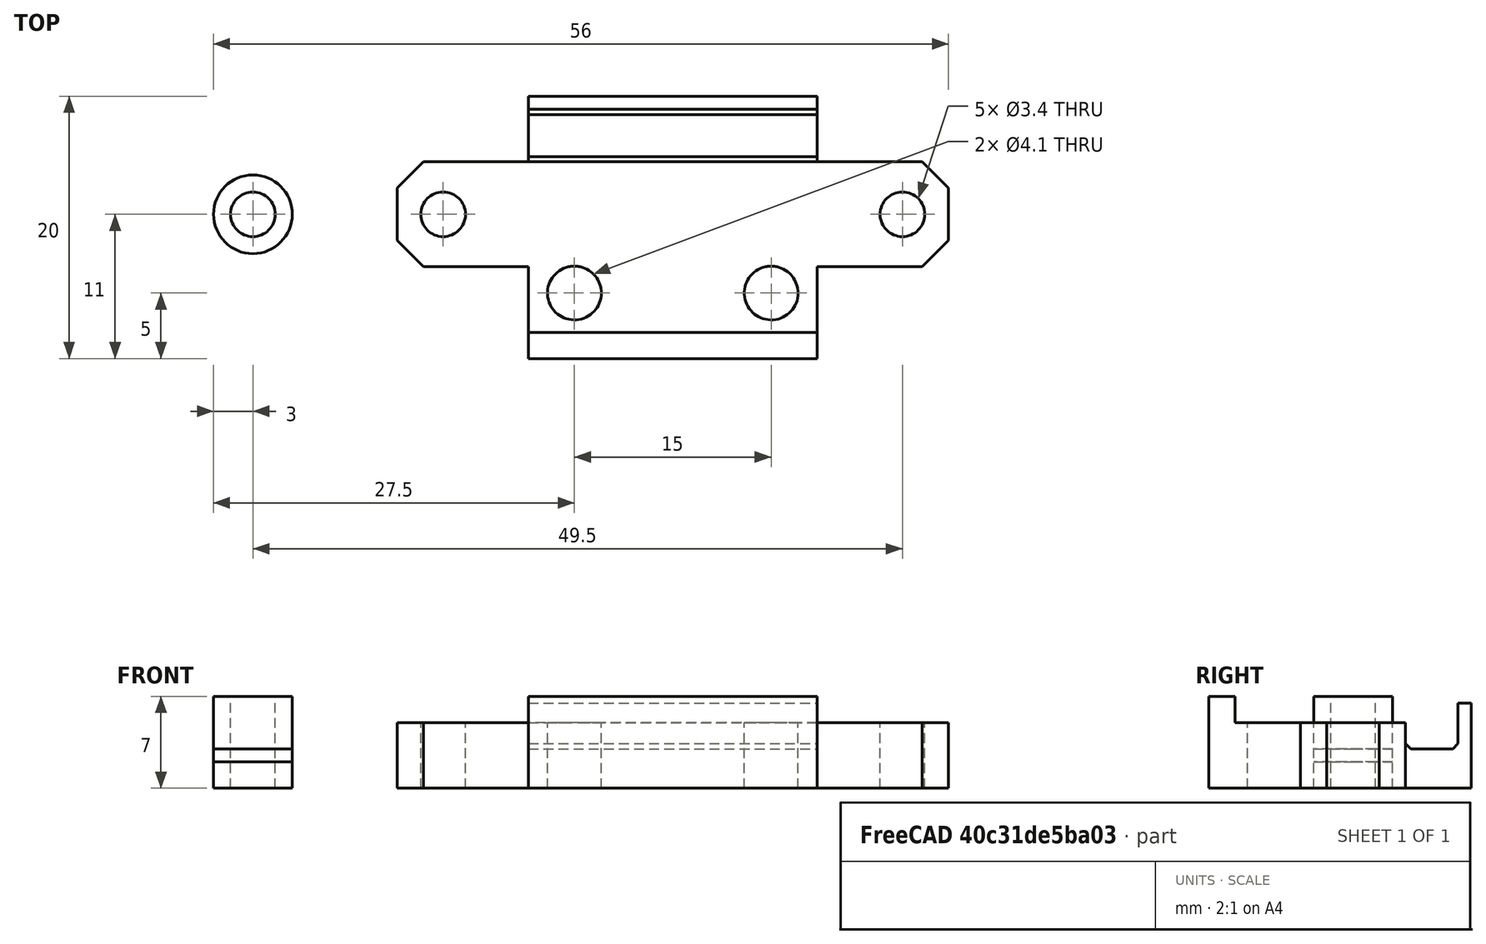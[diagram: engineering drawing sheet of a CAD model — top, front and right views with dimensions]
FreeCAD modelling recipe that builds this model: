
FCSTD DOCUMENT  (FreeCAD 0.18R16146 (Git))
Label: ASDL345-sensor-mount
License: All rights reserved
LicenseURL: http://en.wikipedia.org/wiki/All_rights_reserved
objects: Part::Cylinder×10, Part::Cut×6, Part::Box×3, Part::MultiFuse×3, Part::Feature×1, Part::Chamfer×1
note: 24 computed .brp shape members not serialized (recipe doc carries the construction recipe); baked Part::Feature solids carry a one-line shape summary decoded from their .brp

FEATURE [Part::Feature] Chamfer002001  label="sensor-r002"
  Placement = pos=(0,-7,5) rot=(0,0,1;0rad)
  shape: bbox 22 x 28 x 6 mm, 33 faces (baked)
FEATURE [Part::Box] Box  label="Cube"
  AttacherType = Attacher::AttachEngine3D
  Height = 5
  Length = 42
  Placement = pos=(-21,-4,0) rot=(0,0,1;0rad)
  Width = 8
FEATURE [Part::Cylinder] Cylinder
  Angle = 360
  AttacherType = Attacher::AttachEngine3D
  Height = 10
  Placement = pos=(-17.5,0,0) rot=(0,0,1;0rad)
  Radius = 1.7
FEATURE [Part::Cylinder] Cylinder001
  Angle = 360
  AttacherType = Attacher::AttachEngine3D
  Height = 10
  Placement = pos=(17.5,0,0) rot=(0,0,1;0rad)
  Radius = 1.7
FEATURE [Part::MultiFuse] Fusion
  Shapes = -> [Cylinder,Cylinder001]
FEATURE [Part::Cut] Cut
  Base = -> Box
  Tool = -> Fusion
FEATURE [Part::Chamfer] Chamfer
  Base = -> Cut
  Edges = 4 edges r=2: [Edge1,Edge3,Edge6,Edge13]
FEATURE [Part::Box] Box001  label="Cube001"
  AttacherType = Attacher::AttachEngine3D
  Height = 2
  Length = 22
  Placement = pos=(-11,-11,0) rot=(0,0,1;0rad)
  Width = 20
FEATURE [Part::Box] Box002  label="Cube002"
  AttacherType = Attacher::AttachEngine3D
  Height = 13
  Length = 22
  Placement = pos=(-11,11,0) rot=(0,0,1;0rad)
  Width = 20
FEATURE [Part::Cut] Cut001
  Base = -> Chamfer002001
  Placement = pos=(0,-2,0) rot=(0,0,1;0rad)
  Tool = -> Box002
FEATURE [Part::Cylinder] Cylinder002
  Angle = 360
  AttacherType = Attacher::AttachEngine3D
  Height = 10
  Placement = pos=(-7.5,-6,0) rot=(0,0,1;0rad)
  Radius = 2.05
FEATURE [Part::Cylinder] Cylinder003
  Angle = 360
  AttacherType = Attacher::AttachEngine3D
  Height = 10
  Placement = pos=(7.5,-6,0) rot=(0,0,1;0rad)
  Radius = 2.05
FEATURE [Part::MultiFuse] Fusion001
  Placement = pos=(0,0,-1.5) rot=(0,0,1;0rad)
  Shapes = -> [Cylinder002,Cylinder003]
FEATURE [Part::MultiFuse] Fusion002
  Shapes = -> [Cut001,Box001,Chamfer]
FEATURE [Part::Cut] Cut002
  Base = -> Fusion002
  Tool = -> Fusion001
FEATURE [Part::Cylinder] Cylinder004
  Angle = 360
  AttacherType = Attacher::AttachEngine3D
  Height = 7
  Placement = pos=(-32,0,0) rot=(0,0,1;0rad)
  Radius = 3
FEATURE [Part::Cylinder] Cylinder005
  Angle = 360
  AttacherType = Attacher::AttachEngine3D
  Height = 7
  Placement = pos=(-32,0,0) rot=(0,0,1;0rad)
  Radius = 1.7
FEATURE [Part::Cylinder] Cylinder006
  Angle = 360
  AttacherType = Attacher::AttachEngine3D
  Height = 2
  Placement = pos=(-32,0,0) rot=(0,0,1;0rad)
  Radius = 1.7
FEATURE [Part::Cylinder] Cylinder007
  Angle = 360
  AttacherType = Attacher::AttachEngine3D
  Height = 2
  Placement = pos=(-32,0,0) rot=(0,0,1;0rad)
  Radius = 3
FEATURE [Part::Cylinder] Cylinder008
  Angle = 360
  AttacherType = Attacher::AttachEngine3D
  Height = 3
  Placement = pos=(-32,0,0) rot=(0,0,1;0rad)
  Radius = 3
FEATURE [Part::Cylinder] Cylinder009
  Angle = 360
  AttacherType = Attacher::AttachEngine3D
  Height = 3
  Placement = pos=(-32,0,0) rot=(0,0,1;0rad)
  Radius = 1.7
FEATURE [Part::Cut] Cut003  label="7mm-spc"
  Base = -> Cylinder004
  Tool = -> Cylinder005
FEATURE [Part::Cut] Cut004  label="3mm-spc"
  Base = -> Cylinder008
  Tool = -> Cylinder009
FEATURE [Part::Cut] Cut005  label="2mm-spc"
  Base = -> Cylinder007
  Tool = -> Cylinder006
